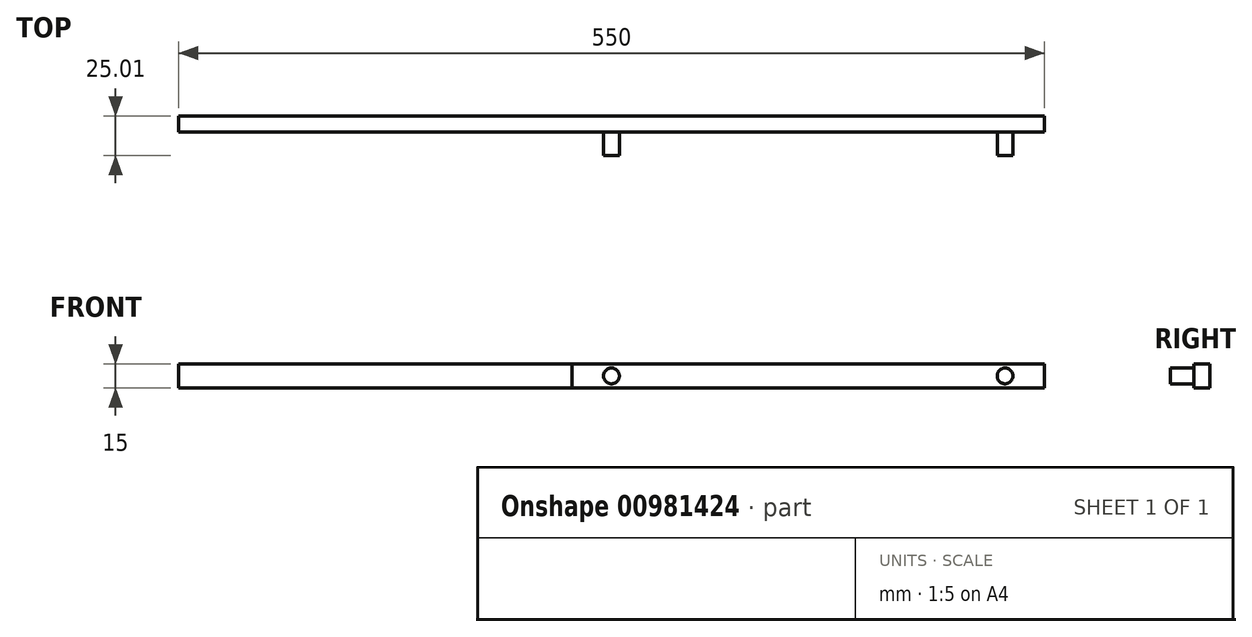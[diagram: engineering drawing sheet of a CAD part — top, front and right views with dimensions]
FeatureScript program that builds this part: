
annotation { "Feature Type Name" : "Feature", "Feature Type Description" : "" }
export const myFeature = defineFeature(function(context is Context, id is Id, definition is map)
    precondition{}
    {
        {
            var Q0;
            Q0=qCreatedBy(makeId("Front.planeOp"),FACE);
            var sketch = newSketch(context, id + "F0", { "sketchPlane" : qUnion([Q0])});
            skLineSegment(sketch, "E0.bottom", {"start": v(-150, 7.5) * mm, "end": v(150, 7.5) * mm});
            skLineSegment(sketch, "E0.top", {"start": v(-150, -7.5) * mm, "end": v(150, -7.5) * mm});
            skLineSegment(sketch, "E0.left", {"start": v(-150, 7.5) * mm, "end": v(-150, -7.5) * mm});
            skLineSegment(sketch, "E0.right", {"start": v(150, 7.5) * mm, "end": v(150, -7.5) * mm});
            skPoint(sketch, "E0.middle", {"position": v(0, 0) * mm});
            skPoint(sketch, "E1", {"position": v(-125, 0) * mm});
            skPoint(sketch, "E2", {"position": v(125, 0) * mm});
            skCircle(sketch, "E3", {"center": v(-125, 0) * mm, "radius": 5 * mm});
            skCircle(sketch, "E4", {"center": v(125, 0) * mm, "radius": 5 * mm});
            skSolve(sketch);
        }
        {
            var Q0;
            Q0=makeQuery(id+"F0.imprint","IMPRINT",FACE,{"disambiguationData":[TD([[makeQuery(id+"F0.imprint","IMPRINT",EDGE,{"derivedFrom":sQuery(id+"F0.wireOp",EDGE,"E0.bottom")}),-1.0]])]});
            extrude(context, id + "F1", {"entities" : qUnion([Q0]), "depth" : 10 * mm, "offsetDistance" : 25 * mm});
        }
        {
            var Q0;
            Q0=makeQuery(id+"F0.imprint","IMPRINT",FACE,{"disambiguationData":[TD([[makeQuery(id+"F0.imprint","IMPRINT",EDGE,{"derivedFrom":sQuery(id+"F0.wireOp",EDGE,"E3")}),1.0]])]});
            var Q1;
            Q1=makeQuery(id+"F0.imprint","IMPRINT",FACE,{"disambiguationData":[TD([[makeQuery(id+"F0.imprint","IMPRINT",EDGE,{"derivedFrom":sQuery(id+"F0.wireOp",EDGE,"E4")}),1.0]])]});
            extrude(context, id + "F2", {"entities" : qUnion([Q0, Q1]), "operationType" : NewBodyOperationType.ADD, "depth" : 25 * mm, "offsetDistance" : 25 * mm});
        }
        {
            var Q0;
            Q0=makeQuery(id+"F1.opExtrude","SWEPT_FACE",FACE,{"disambiguationData":[OSD([sQuery(id+"F0.wireOp",EDGE,"E0.left")])]});
            cPlane(context, id + "F3", {"entities" : qUnion([Q0]), "cplaneType" : CPlaneType.OFFSET, "offset" : 0 * mm, "width" : 150 * mm, "height" : 150 * mm});
        }
        {
            var Q0;
            Q0=qCreatedBy(id+"F3.planeOp",FACE);
            var sketch = newSketch(context, id + "F4", { "sketchPlane" : qUnion([Q0])});
            skLineSegment(sketch, "E5.bottom", {"start": v(-0.01, 7.5) * mm, "end": v(9.99, 7.5) * mm});
            skLineSegment(sketch, "E5.top", {"start": v(-0.01, -7.5) * mm, "end": v(9.99, -7.5) * mm});
            skLineSegment(sketch, "E5.left", {"start": v(-0.01, 7.5) * mm, "end": v(-0.01, -7.5) * mm});
            skLineSegment(sketch, "E5.right", {"start": v(9.99, 7.5) * mm, "end": v(9.99, -7.5) * mm});
            skPoint(sketch, "E5.middle", {"position": v(4.99, 0) * mm});
            skSolve(sketch);
        }
        {
            var Q0;
            Q0 = qSketchRegion(id + "F4", true);
            extrude(context, id + "F5", {"entities" : qUnion([Q0]), "operationType" : NewBodyOperationType.ADD, "depth" : 250 * mm, "offsetDistance" : 25 * mm});
        }
    });
